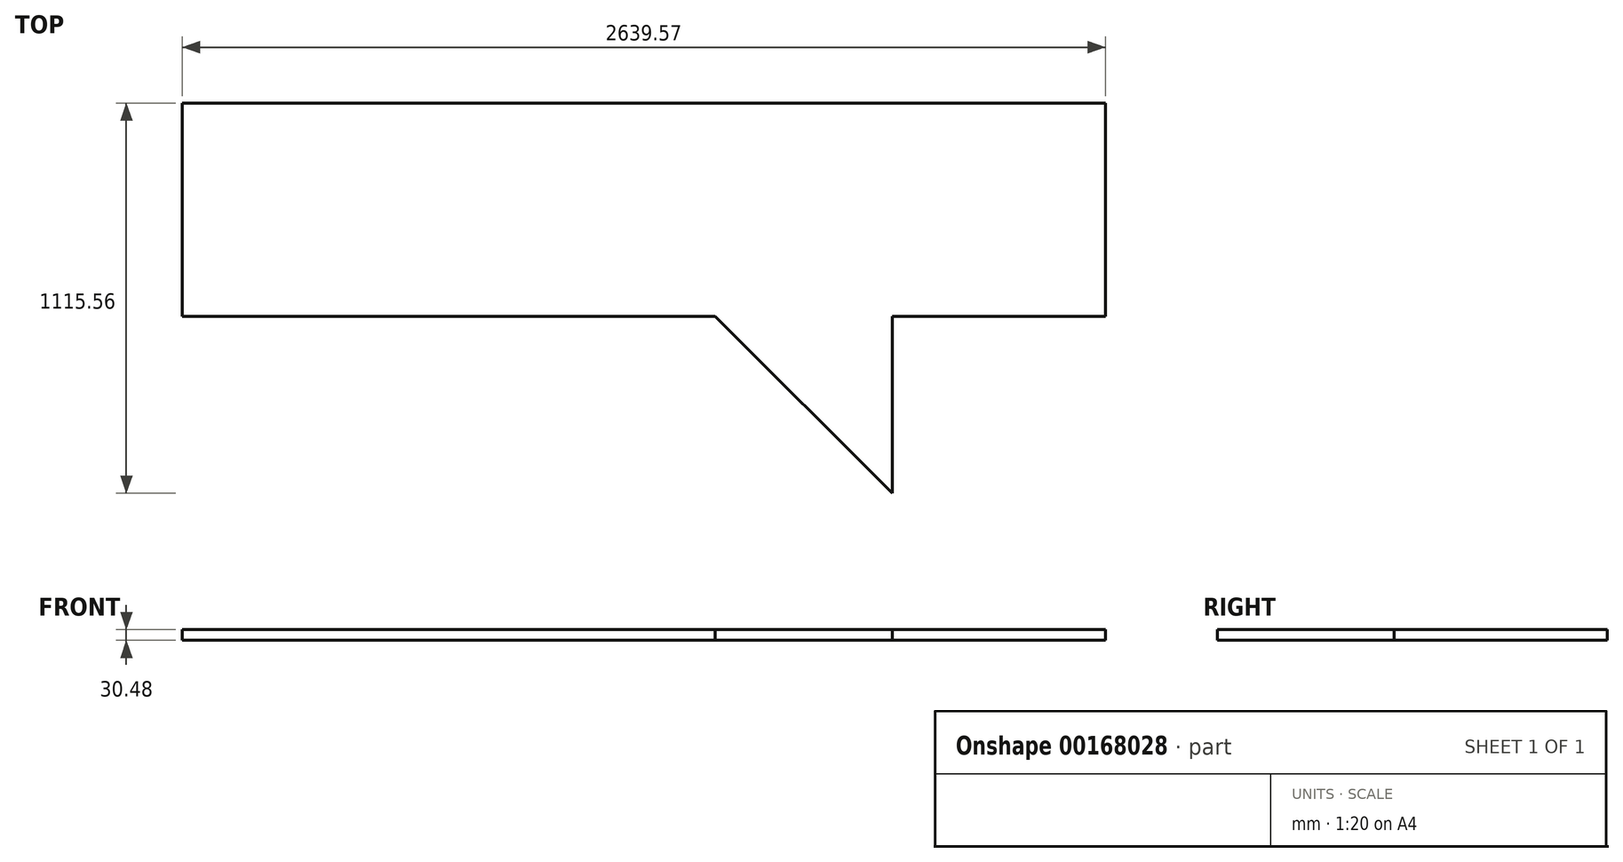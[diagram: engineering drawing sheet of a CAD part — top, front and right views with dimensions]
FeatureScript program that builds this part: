
annotation { "Feature Type Name" : "Feature", "Feature Type Description" : "" }
export const myFeature = defineFeature(function(context is Context, id is Id, definition is map)
    precondition{}
    {
        {
            var Q0;
            Q0=qCreatedBy(makeId("Top.planeOp"),FACE);
            var sketch = newSketch(context, id + "F0", { "sketchPlane" : qUnion([Q0])});
            skLineSegment(sketch, "E0.bottom", {"start": v(-1523.84, 1800.47) * mm, "end": v(1524.16, 1800.47) * mm});
            skLineSegment(sketch, "E0.top", {"start": v(-1523.84, -1552.33) * mm, "end": v(1524.16, -1552.33) * mm});
            skLineSegment(sketch, "E0.left", {"start": v(-1523.84, 1800.47) * mm, "end": v(-1523.84, -1552.33) * mm});
            skLineSegment(sketch, "E0.right", {"start": v(1524.16, 1800.47) * mm, "end": v(1524.16, -1552.33) * mm});
            skSolve(sketch);
        }
        {
            var Q0;
            Q0=qCreatedBy(makeId("Top.planeOp"),FACE);
            var sketch = newSketch(context, id + "F1", { "sketchPlane" : qUnion([Q0])});
            skLineSegment(sketch, "E1.bottom", {"start": v(-1382.11, 1609.97) * mm, "end": v(1257.46, 1609.97) * mm});
            skLineSegment(sketch, "E1.top", {"start": v(-1382.11, 1000.37) * mm, "end": v(1257.46, 1000.37) * mm});
            skLineSegment(sketch, "E1.left", {"start": v(-1382.11, 1609.97) * mm, "end": v(-1382.11, 1000.37) * mm});
            skLineSegment(sketch, "E1.right", {"start": v(1257.46, 1609.97) * mm, "end": v(1257.46, 1000.37) * mm});
            skLineSegment(sketch, "E2.bottom", {"start": v(647.86, 1000.37) * mm, "end": v(1257.46, 1000.37) * mm});
            skLineSegment(sketch, "E2.top", {"start": v(647.86, -1029.6) * mm, "end": v(1257.46, -1029.6) * mm});
            skLineSegment(sketch, "E2.left", {"start": v(647.86, 1000.37) * mm, "end": v(647.86, -1029.6) * mm});
            skLineSegment(sketch, "E2.right", {"start": v(1257.46, 1000.37) * mm, "end": v(1257.46, -1029.6) * mm});
            skLineSegment(sketch, "E3", {"start": v(141.89, 1000.37) * mm, "end": v(647.86, 494.4) * mm});
            skSolve(sketch);
        }
        {
            var Q0;
            Q0=makeQuery(id+"F1.imprint","IMPRINT",FACE,{"disambiguationData":[TD([[makeQuery(id+"F1.imprint","IMPRINT",EDGE,{"derivedFrom":sQuery(id+"F1.wireOp",EDGE,"E1.bottom")}),-1.0]])]});
            var Q1;
            {var subQ3=sQuery(id+"F1.wireOp",EDGE,"E3");Q1=makeQuery(id+"F1.imprint","IMPRINT",FACE,{"disambiguationData":[TD([[makeQuery(id+"F1.imprint","IMPRINT",EDGE,{"derivedFrom":subQ3}),1.0]])]});}
            var Q2;
            {var subQ3=sQuery(id+"F1.wireOp",EDGE,"E2.bottom");Q2=makeQuery(id+"F1.imprint","IMPRINT",FACE,{"disambiguationData":[TD([[makeQuery(id+"F1.imprint","IMPRINT",EDGE,{"derivedFrom":subQ3}),-1.0]])]});}
            var Q3;
            Q3=sQuery(id+"F1.wireOp",EDGE,"E2.right");
            var Q4;
            Q4=sQuery(id+"F1.wireOp",EDGE,"E3");
            var Q5;
            Q5=sQuery(id+"F1.wireOp",EDGE,"E1.bottom");
            var Q6;
            Q6=sQuery(id+"F1.wireOp",EDGE,"E2.left");
            var Q7;
            Q7=sQuery(id+"F1.wireOp",EDGE,"E1.top");
            var Q8;
            Q8=sQuery(id+"F1.wireOp",EDGE,"E2.top");
            var Q9;
            Q9=sQuery(id+"F1.wireOp",EDGE,"E1.left");
            var Q10;
            Q10=sQuery(id+"F1.wireOp",EDGE,"E1.right");
            var Q11;
            Q11=sQuery(id+"F1.wireOp",EDGE,"E2.bottom");
            extrude(context, id + "F2", {"entities" : qUnion([Q0, Q1, Q2]), "surfaceEntities" : qUnion([Q3, Q4, Q5, Q6, Q7, Q8, Q9, Q10, Q11]), "depth" : 30.48 * mm});
        }
    });
